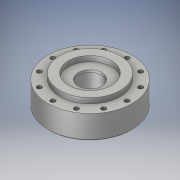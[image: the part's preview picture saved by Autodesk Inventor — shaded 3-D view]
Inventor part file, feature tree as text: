
AUTODESK INVENTOR PART (.ipt)
format: ipt  version: 2018 (Build 220112000, 112)  size: 233,984 bytes
history: native  units: in
note: dims shown in document units (in); Inventor stores cm internally (conversion verified against a paired STEP export)
features: sketch x8, extrude x7, chamfer x2, hole x1, pattern_circular x1
ambient origin geometry x8: Origin, YZ Plane, XZ Plane, XY Plane, X Axis, Y Axis, Z Axis, Center Point
bodies: Solid1 (feature_tree)
feature tree (19):
  extrude  "Extrusion1"  Depth=0.5in TaperAngle=0.0deg
  chamfer  "Chamfer1"  Distance=0.0291in Angle=45.0deg
  extrude  "Extrusion2"  Depth=0.113in TaperAngle=0.0deg
  extrude  "Extrusion3"  Depth=0.05in
  hole  "Hole1"  [1 undecoded]
  chamfer  "Chamfer3"  Distance=0.007in Angle=45.0deg
  extrude  "Extrusion6"  Depth=1.0in TaperAngle=0.0deg
  pattern_circular  "Circular Pattern2"  Count=12 Angle=360.0deg
  extrude  "Extrusion10"  Depth=0.45in
  extrude  "Extrusion11"  Depth=0.1in TaperAngle=0.0deg
  sketch  "Sketch1"  dims[d0=1.755in d1=0.5in d2=0.0in d3=0.0291in d4=0.125in d5=45.0deg]
  sketch  "Sketch2"  dims[d6=1.26in d7=0.113in d8=0.0in]
  sketch  "Sketch3"  dims[d9=0.658in d10=0.05in]
  sketch  "Sketch6"  dims[d11=0.04in d12=0.0in d22=0.775in]
  sketch  "Sketch7"  dims[d23=30.0deg]
  sketch  "Sketch11"  dims[d37=0.9in d38=1.0in d39=0.0in]
  sketch  "Sketch12"  dims[d45=0.495in d47=0.0in d48=0.04in d52=4.7244in d53=360.0deg d55=0.51in d56=0.1in d57=0.0in d58=0.501in d59=0.45in d60=0.0in]
  sketch  "Sketch9"  dims[d24=0.085in d25=0.224in d26=0.375in d27=0.25in d28=0.5635in d29=0.349in d30=0.8108in d31=0.007in d32=0.125in d33=45.0deg]
  extrude  "Extrusion8"  Depth=0.45in
note: 1 required parameter value undecoded (feature->parameter linkage not recoverable at this tier; creation-order binding heuristic only, values carry confidence <= 0.55)
